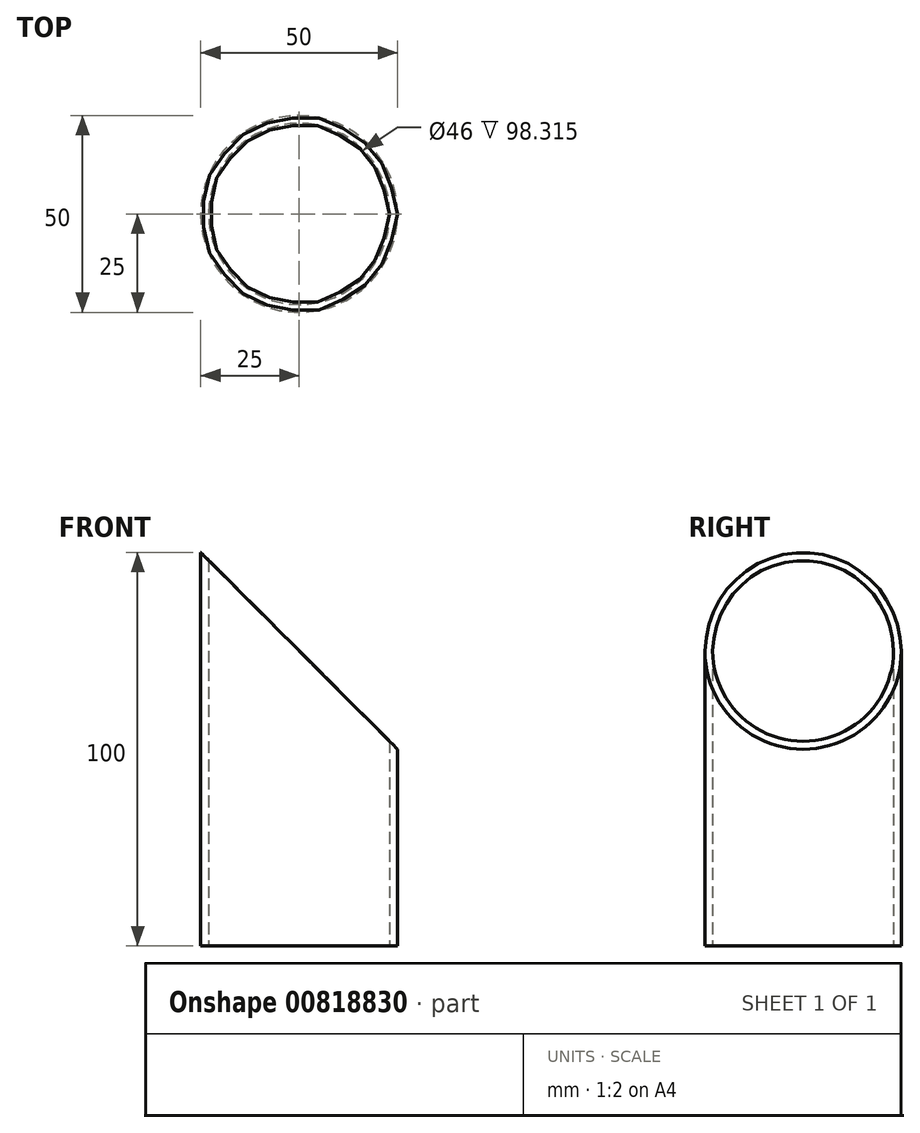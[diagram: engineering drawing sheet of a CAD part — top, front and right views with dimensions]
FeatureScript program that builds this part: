
annotation { "Feature Type Name" : "Feature", "Feature Type Description" : "" }
export const myFeature = defineFeature(function(context is Context, id is Id, definition is map)
    precondition{}
    {
        {
            var Q0;
            Q0=qCreatedBy(makeId("Top.planeOp"),FACE);
            var sketch = newSketch(context, id + "F0", { "sketchPlane" : qUnion([Q0])});
            skCircle(sketch, "E0", {"center": v(0, 0) * mm, "radius": 25 * mm});
            skCircle(sketch, "E1", {"center": v(0, 0) * mm, "radius": 23 * mm});
            skSolve(sketch);
        }
        {
            var Q0;
            Q0=makeQuery(id+"F0.imprint","IMPRINT",FACE,{"disambiguationData":[TD([[makeQuery(id+"F0.imprint","IMPRINT",EDGE,{"derivedFrom":sQuery(id+"F0.wireOp",EDGE,"E0")}),1.0]])]});
            extrude(context, id + "F1", {"entities" : qUnion([Q0]), "depth" : 100 * mm, "offsetDistance" : 25 * mm});
        }
        {
            var Q0;
            Q0=qCreatedBy(makeId("Front.planeOp"),FACE);
            var sketch = newSketch(context, id + "F2", { "sketchPlane" : qUnion([Q0])});
            skLineSegment(sketch, "E2.0", {"start": v(-25, 100) * mm, "end": v(25, 100) * mm});
            skLineSegment(sketch, "E3", {"start": v(25, 100) * mm, "end": v(25, 50) * mm});
            skLineSegment(sketch, "E4", {"start": v(-25, 100) * mm, "end": v(25, 50) * mm});
            skPoint(sketch, "E5.0.start.orphan", {"position": v(-25, 0) * mm});
            skPoint(sketch, "E6.orphan", {"position": v(25, 0) * mm});
            skLineSegment(sketch, "E7", {"start": v(25, 50) * mm, "end": v(25, 100) * mm});
            skSolve(sketch);
        }
        {
            var Q0;
            Q0 = qSketchRegion(id + "F2", true);
            extrude(context, id + "F3", {"entities" : qUnion([Q0]), "operationType" : NewBodyOperationType.REMOVE, "endBound" : BoundingType.THROUGH_ALL, "depth" : 25 * mm, "offsetDistance" : 25 * mm, "hasSecondDirection" : true, "secondDirectionBound" : SecondDirectionBoundingType.THROUGH_ALL, "secondDirectionOppositeDirection" : true, "secondDirectionDepth" : 25 * mm});
        }
        {
            var Q0;
            Q0=makeQuery(id+"F3.boolean.opBoolean","COPY",FACE,{"derivedFrom":makeQuery(id+"F3.opExtrude","SWEPT_FACE",FACE,{"disambiguationData":[OSD([sQuery(id+"F2.wireOp",EDGE,"E4")])]})});
            cPlane(context, id + "F4", {"entities" : qUnion([Q0]), "cplaneType" : CPlaneType.OFFSET, "offset" : 0 * mm, "width" : 150 * mm, "height" : 150 * mm});
        }
        {
            var Q0;
            Q0=qCreatedBy(id+"F4.planeOp",FACE);
            var sketch = newSketch(context, id + "F5", { "sketchPlane" : qUnion([Q0])});
            skEllipse(sketch, "E8.0", {"center": v(-53.03, 0) * mm, "majorRadius": 32.53 * mm, "minorRadius": 23 * mm, "majorAxis": v(1, 0)});
            skEllipse(sketch, "E9.0", {"center": v(-53.03, 0) * mm, "majorRadius": 35.36 * mm, "minorRadius": 25 * mm, "majorAxis": v(1, 0)});
            skSolve(sketch);
        }
    });
